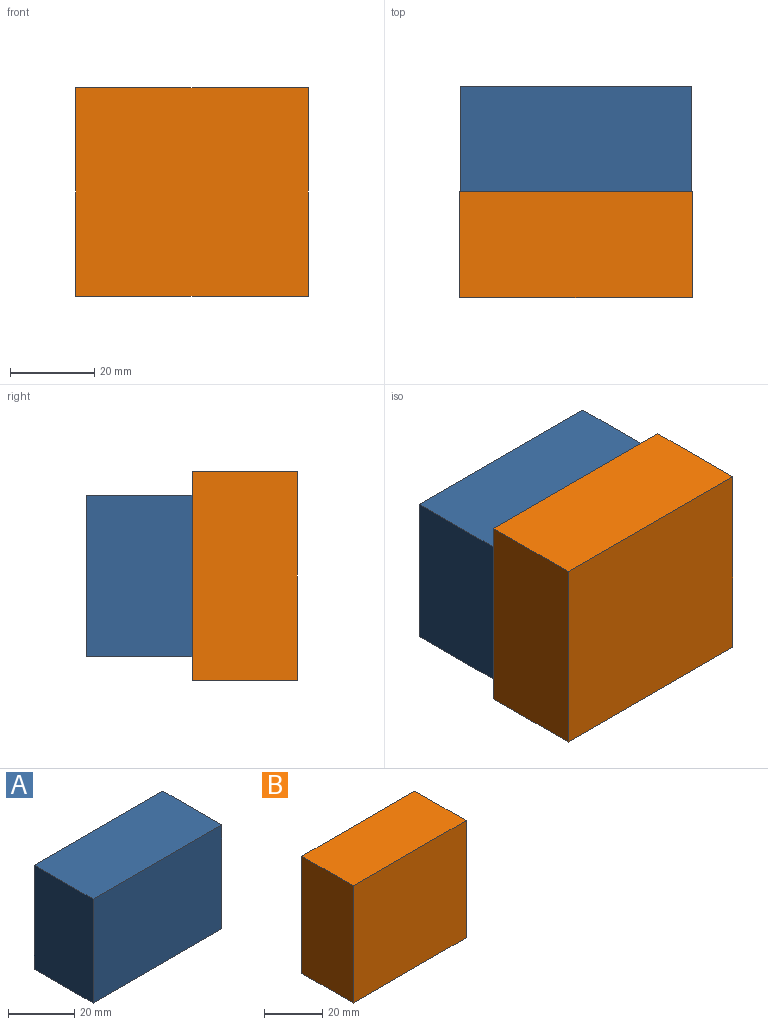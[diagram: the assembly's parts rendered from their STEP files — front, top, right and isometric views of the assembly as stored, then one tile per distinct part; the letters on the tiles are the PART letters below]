
ASSEMBLY  parts=2 mates=1
PART A: 6 faces, bbox 54.8x25x38.4 mm
  f0: plane 54.75x25mm, normal (0,0,1), area 1368.8mm2, adj f1,f3,f4,f5
  f1: plane 38.36x25mm, normal (-1,0,0), area 959mm2, adj f0,f2,f4,f5
  f2: plane 54.75x25mm, normal (0,0,-1), area 1368.8mm2, adj f1,f3,f4,f5
  f3: plane 38.36x25mm, normal (1,0,0), area 959mm2, adj f0,f2,f4,f5
  f4: plane 54.75x38.36mm, normal (0,-1,0), area 2100.3mm2, adj f0,f1,f2,f3
  f5: plane 54.75x38.36mm, normal (0,1,0), area 2100.3mm2, adj f0,f1,f2,f3
PART B: 6 faces, bbox 55x25x49.5 mm
  f0: plane 55.05x25mm, normal (0,0,1), area 1376.2mm2, adj f1,f3,f4,f5
  f1: plane 49.46x25mm, normal (-1,0,0), area 1236.5mm2, adj f0,f2,f4,f5
  f2: plane 55.05x25mm, normal (0,0,-1), area 1376.2mm2, adj f1,f3,f4,f5
  f3: plane 49.46x25mm, normal (1,0,0), area 1236.5mm2, adj f0,f2,f4,f5
  f4: plane 55.05x49.46mm, normal (0,-1,0), area 2722.7mm2, adj f0,f1,f2,f3
  f5: plane 55.05x49.46mm, normal (0,1,0), area 2722.7mm2, adj f0,f1,f2,f3
PLACE A at identity fixed
PLACE B rot(axis=(1,0,0),180deg) t=(-124.96,-50,41.91)mm
MATE fastened B.f4 <-> A.f4  axis (0,1,0) through (-37.83,-25,33.53)mm
